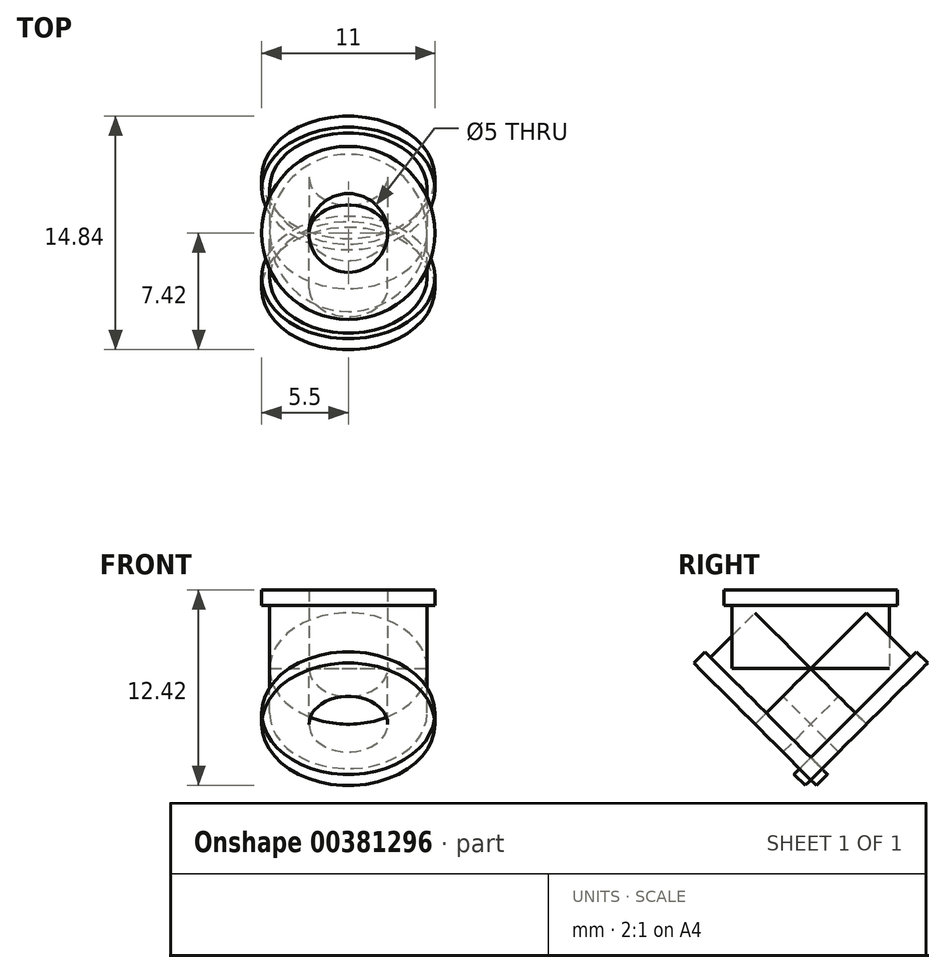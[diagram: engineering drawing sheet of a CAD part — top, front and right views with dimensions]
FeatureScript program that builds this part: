
annotation { "Feature Type Name" : "Feature", "Feature Type Description" : "" }
export const myFeature = defineFeature(function(context is Context, id is Id, definition is map)
    precondition{}
    {
        {
            var Q0;
            Q0=qCreatedBy(makeId("Front.planeOp"),FACE);
            var sketch = newSketch(context, id + "F0", { "sketchPlane" : qUnion([Q0])});
            skLineSegment(sketch, "E0", {"start": v(0, 0) * mm, "end": v(0, 5.18) * mm, "construction": true});
            skLineSegment(sketch, "E1", {"start": v(2.5, 0) * mm, "end": v(2.5, 5) * mm});
            skLineSegment(sketch, "E2", {"start": v(2.5, 5) * mm, "end": v(5.5, 5) * mm});
            skLineSegment(sketch, "E3", {"start": v(5.5, 5) * mm, "end": v(5.5, 4) * mm});
            skLineSegment(sketch, "E4", {"start": v(5.5, 4) * mm, "end": v(5, 4) * mm});
            skLineSegment(sketch, "E5", {"start": v(5, 4) * mm, "end": v(5, 0) * mm});
            skLineSegment(sketch, "E6", {"start": v(5, 0) * mm, "end": v(2.5, 0) * mm});
            skSolve(sketch);
        }
        {
            var Q0;
            Q0=makeQuery(id+"F0.imprint","IMPRINT",FACE,{"disambiguationData":[TD([[makeQuery(id+"F0.imprint","IMPRINT",EDGE,{"derivedFrom":sQuery(id+"F0.wireOp",EDGE,"E1")}),-1.0]])]});
            var Q1;
            Q1=sQuery(id+"F0.wireOp",EDGE,"E0");
            revolve(context, id + "F1", {"entities" : qUnion([Q0]), "axis" : qUnion([Q1]), "revolveType" : RevolveType.FULL});
        }
        {
            var Q0;
            Q0=qCreatedBy(makeId("Front.planeOp"),FACE);
            var sketch = newSketch(context, id + "F2", { "sketchPlane" : qUnion([Q0])});
            skLineSegment(sketch, "E7", {"start": v(0, 0) * mm, "end": v(-18.77, 0) * mm, "construction": true});
            skSolve(sketch);
        }
        {
            var Q0;
            Q0=makeQuery(id+"F1.opRevolve","SWEPT_BODY",BODY,{"disambiguationData":[OSD([sQuery(id+"F0.wireOp",EDGE,"E1"),sQuery(id+"F0.wireOp",EDGE,"E2"),sQuery(id+"F0.wireOp",EDGE,"E3"),sQuery(id+"F0.wireOp",EDGE,"E4"),sQuery(id+"F0.wireOp",EDGE,"E5"),sQuery(id+"F0.wireOp",EDGE,"E6")])]});
            var Q1;
            Q1=sQuery(id+"F2.wireOp",EDGE,"E7");
            transform(context, id + "F3", {"entities" : qUnion([Q0]), "transformType" : TransformType.ROTATION, "transformAxis" : qUnion([Q1]), "angle" : 135 * degree, "makeCopy" : true});
        }
        {
            var Q0;
            Q0=makeQuery(id+"F1.opRevolve","SWEPT_BODY",BODY,{"disambiguationData":[OSD([sQuery(id+"F0.wireOp",EDGE,"E1"),sQuery(id+"F0.wireOp",EDGE,"E2"),sQuery(id+"F0.wireOp",EDGE,"E3"),sQuery(id+"F0.wireOp",EDGE,"E4"),sQuery(id+"F0.wireOp",EDGE,"E5"),sQuery(id+"F0.wireOp",EDGE,"E6")])]});
            var Q1;
            Q1=sQuery(id+"F2.wireOp",EDGE,"E7");
            transform(context, id + "F4", {"entities" : qUnion([Q0]), "transformType" : TransformType.ROTATION, "transformAxis" : qUnion([Q1]), "angle" : 225 * degree, "makeCopy" : true});
        }
    });
